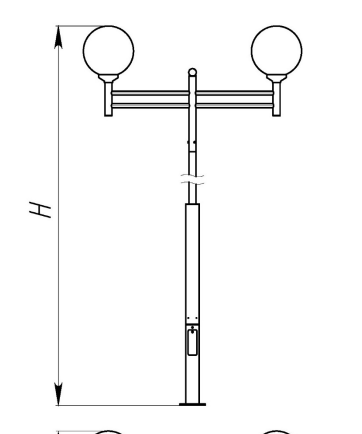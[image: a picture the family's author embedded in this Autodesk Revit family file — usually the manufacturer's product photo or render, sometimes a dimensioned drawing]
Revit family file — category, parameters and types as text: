
# Revit family: Стальной фонарный столб Т-13-2 со светильниками Арт 6958
name_source: partatom
category: Антураж
revit_build: Autodesk Revit 2018 (Build: 20180423_1000(x64)
units: mm (PartAtom-declared; Revit-internal decimal feet)

## family parameters
Всегда вертикально = Да
Источник визуального образа = Геометрия семейства
На основе рабочей плоскости = Нет
Общий = Нет
При загрузке вырезать с полостями = Нет
Точка расчета площади = Нет

## types (6) — shared parameters
URL = https://hobbyka.ru
Артикул товара = Арт. 6958
Группа модели = Светильники со стальными опорами
Длина = 1740 мм
Изготовитель = ООО «Хоббика»
Изображение типоразмера = Стальной фонарный столб Т-13-2 со светильниками Арт 6958.jpg
Материал изделия = Сталь, поликарбонат
Цвет опоры = Сталь
Цвет плафона = Стекло(1)
Ширина = 400 мм

## per-type parameters (varying)
| type | Версия 3,5 м | Версия 4,0 м | Версия 4,5 м | Версия 5,0 м | Версия 5,5 м | Версия 6,0 м | Высота | Описание |
| Версия 3,5 м | Да | Нет | Нет | Нет | Нет | Нет | 3500 мм | Стальной фонарный столб Т-13-2 со светильниками. Версия 3,5 м |
| Версия 4,0 м | Нет | Да | Нет | Нет | Нет | Нет | 4000 мм | Стальной фонарный столб Т-13-2 со светильниками. Версия 4,0 м |
| Версия 4,5 м | Нет | Нет | Да | Нет | Нет | Нет | 4500 мм | Стальной фонарный столб Т-13-2 со светильниками. Версия 4,5 м |
| Версия 5,0 м | Нет | Нет | Нет | Да | Нет | Нет | 5000 мм | Стальной фонарный столб Т-13-2 со светильниками. Версия 5,0 м |
| Версия 5,5 м | Нет | Нет | Нет | Нет | Да | Нет | 5500 мм | Стальной фонарный столб Т-13-2 со светильниками. Версия 5,5 м |
| Версия 6,0 м | Нет | Нет | Нет | Нет | Нет | Да | 6000 мм | Стальной фонарный столб Т-13-2 со светильниками. Версия 6,0 м |
